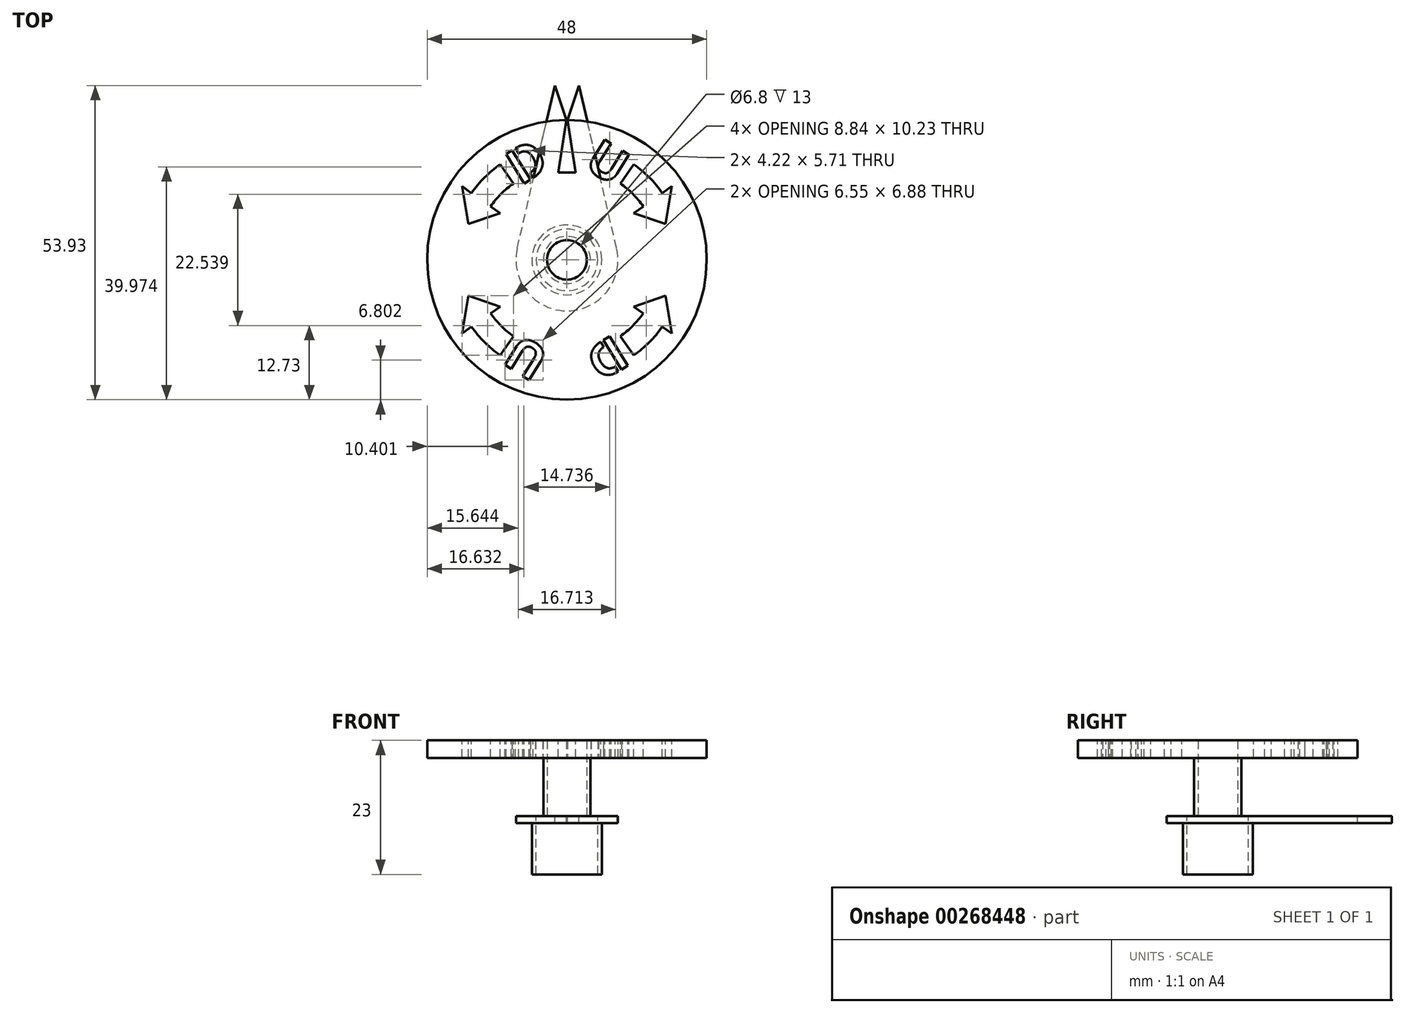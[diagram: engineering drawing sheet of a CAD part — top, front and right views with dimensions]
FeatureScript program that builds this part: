
annotation { "Feature Type Name" : "Feature", "Feature Type Description" : "" }
export const myFeature = defineFeature(function(context is Context, id is Id, definition is map)
    precondition{}
    {
        {
            var Q0;
            Q0=qCreatedBy(makeId("Top.planeOp"),FACE);
            var sketch = newSketch(context, id + "F0", { "sketchPlane" : qUnion([Q0])});
            skCircle(sketch, "E0", {"center": v(0, 0) * mm, "radius": 3.4 * mm});
            skCircle(sketch, "E1", {"center": v(0, 0) * mm, "radius": 4.05 * mm});
            skSolve(sketch);
        }
        {
            var Q0;
            Q0=makeQuery(id+"F0.imprint","IMPRINT",FACE,{"disambiguationData":[TD([[makeQuery(id+"F0.imprint","IMPRINT",EDGE,{"derivedFrom":sQuery(id+"F0.wireOp",EDGE,"E0")}),-1.0]])]});
            extrude(context, id + "F1", {"entities" : qUnion([Q0]), "depth" : 10 * mm, "offsetDistance" : 25 * mm});
        }
        {
            var Q0;
            Q0=makeQuery(id+"F1.opExtrude","CAP_FACE",FACE,{"disambiguationData":[OSD([sQuery(id+"F0.wireOp",EDGE,"E0"),sQuery(id+"F0.wireOp",EDGE,"E1")])],"isStart":false});
            var sketch = newSketch(context, id + "F2", { "sketchPlane" : qUnion([Q0])});
            skCircle(sketch, "E2", {"center": v(0, 0) * mm, "radius": 24 * mm});
            skSolve(sketch);
        }
        {
            var Q0;
            Q0=makeQuery(id+"F2.imprint","IMPRINT",FACE,{"disambiguationData":[TD([[makeQuery(id+"F2.imprint","IMPRINT",EDGE,{"derivedFrom":sQuery(id+"F2.wireOp",EDGE,"E2")}),1.0]])]});
            var Q1;
            Q1=makeQuery(id+"F2.imprint","IMPRINT",FACE,{"disambiguationData":[TD([[makeQuery(id+"F2.imprint","IMPRINT",EDGE,{"derivedFrom":makeQuery(id+"F1.opExtrude","CAP_EDGE",EDGE,{"disambiguationData":[OSD([sQuery(id+"F0.wireOp",EDGE,"E0")])],"isStart":false})}),-1.0]])]});
            extrude(context, id + "F3", {"entities" : qUnion([Q0, Q1]), "operationType" : NewBodyOperationType.ADD, "depth" : 3 * mm, "offsetDistance" : 25 * mm});
        }
        {
            var Q0;
            Q0=makeQuery(id+"F3.opExtrude","CAP_FACE",FACE,{"disambiguationData":[OSD([sQuery(id+"F0.wireOp",EDGE,"E0"),sQuery(id+"F2.wireOp",EDGE,"E2")])],"isStart":false});
            var sketch = newSketch(context, id + "F4", { "sketchPlane" : qUnion([Q0])});
            skLineSegment(sketch, "E3", {"start": v(0, 0) * mm, "end": v(0, 26.54) * mm, "construction": true});
            skLineSegment(sketch, "E4", {"start": v(0, 24.5) * mm, "end": v(-1.5, 15) * mm});
            skLineSegment(sketch, "E5", {"start": v(-1.5, 15) * mm, "end": v(0, 15) * mm});
            skLineSegment(sketch, "E6.MirrorCS", {"start": v(0, 24.5) * mm, "end": v(1.5, 15) * mm});
            skLineSegment(sketch, "E7.MirrorCS", {"start": v(1.5, 15) * mm, "end": v(0, 15) * mm});
            skLineSegment(sketch, "E8", {"start": v(0, 0) * mm, "end": v(22.55, 8.2) * mm, "construction": true});
            skCircle(sketch, "E9", {"center": v(0, 0) * mm, "radius": 18 * mm, "construction": true});
            skLineSegment(sketch, "E10", {"start": v(0, 0) * mm, "end": v(13.77, 19.66) * mm, "construction": true});
            skLineSegment(sketch, "E11", {"start": v(0, 0) * mm, "end": v(19.66, 13.77) * mm, "construction": true});
            skLineSegment(sketch, "E12", {"start": v(10.32, 14.74) * mm, "end": v(11.47, 16.38) * mm});
            skLineSegment(sketch, "E13", {"start": v(10.32, 14.74) * mm, "end": v(9.18, 13.1) * mm});
            skLineSegment(sketch, "E14", {"start": v(11.47, 8.03) * mm, "end": v(13.1, 9.18) * mm});
            skLineSegment(sketch, "E15", {"start": v(13.1, 9.18) * mm, "end": v(14.74, 10.32) * mm});
            skLineSegment(sketch, "E16", {"start": v(14.74, 10.32) * mm, "end": v(16.38, 11.47) * mm});
            skLineSegment(sketch, "E17", {"start": v(16.38, 11.47) * mm, "end": v(18.02, 12.62) * mm});
            skLineSegment(sketch, "E18", {"start": v(11.47, 8.03) * mm, "end": v(16.91, 6.16) * mm});
            skLineSegment(sketch, "E19", {"start": v(16.91, 6.16) * mm, "end": v(18.02, 12.62) * mm});
            skArc(sketch, "E20", {"start": v(13.1, 9.18) * mm, "mid": v(11.31, 11.31) * mm, "end": v(9.18, 13.1) * mm});
            skArc(sketch, "E21", {"start": v(16.38, 11.47) * mm, "mid": v(14.14, 14.14) * mm, "end": v(11.47, 16.38) * mm});
            skText(sketch, "E22", { "text": "U\n", "fontName": "OpenSans-Bold.ttf"});
            skLineSegment(sketch, "E23", {"start": v(0, 0) * mm, "end": v(27.05, 0) * mm, "construction": true});
            skLineSegment(sketch, "E24.MirrorCS", {"start": v(11.47, -8.03) * mm, "end": v(16.91, -6.16) * mm});
            skLineSegment(sketch, "E25.MirrorCS", {"start": v(16.91, -6.16) * mm, "end": v(18.02, -12.62) * mm});
            skArc(sketch, "E26.MirrorCS", {"start": v(13.1, -9.18) * mm, "mid": v(11.31, -11.31) * mm, "end": v(9.18, -13.1) * mm});
            skArc(sketch, "E27.MirrorCS", {"start": v(16.38, -11.47) * mm, "mid": v(14.14, -14.14) * mm, "end": v(11.47, -16.38) * mm});
            skLineSegment(sketch, "E28.MirrorCS", {"start": v(10.32, -14.74) * mm, "end": v(9.18, -13.1) * mm});
            skLineSegment(sketch, "E29.MirrorCS", {"start": v(10.32, -14.74) * mm, "end": v(11.47, -16.38) * mm});
            skLineSegment(sketch, "E30.MirrorCS", {"start": v(11.47, -8.03) * mm, "end": v(13.1, -9.18) * mm});
            skLineSegment(sketch, "E31.MirrorCS", {"start": v(16.38, -11.47) * mm, "end": v(18.02, -12.62) * mm});
            skLineSegment(sketch, "E32.MirrorCS", {"start": v(-10.32, -14.74) * mm, "end": v(-9.18, -13.1) * mm});
            skLineSegment(sketch, "E33.MirrorCS", {"start": v(-10.32, -14.74) * mm, "end": v(-11.47, -16.38) * mm});
            skArc(sketch, "E34.MirrorCS", {"start": v(-16.38, -11.47) * mm, "mid": v(-14.14, -14.14) * mm, "end": v(-11.47, -16.38) * mm});
            skLineSegment(sketch, "E35.MirrorCS", {"start": v(-16.38, -11.47) * mm, "end": v(-18.02, -12.62) * mm});
            skLineSegment(sketch, "E36.MirrorCS", {"start": v(-16.91, -6.16) * mm, "end": v(-18.02, -12.62) * mm});
            skLineSegment(sketch, "E37.MirrorCS", {"start": v(-11.47, -8.03) * mm, "end": v(-16.91, -6.16) * mm});
            skLineSegment(sketch, "E38.MirrorCS", {"start": v(-11.47, -8.03) * mm, "end": v(-13.1, -9.18) * mm});
            skArc(sketch, "E39.MirrorCS", {"start": v(-13.1, -9.18) * mm, "mid": v(-11.31, -11.31) * mm, "end": v(-9.18, -13.1) * mm});
            skLineSegment(sketch, "E40.MirrorCS", {"start": v(-16.91, 6.16) * mm, "end": v(-18.02, 12.62) * mm});
            skLineSegment(sketch, "E41.MirrorCS", {"start": v(-11.47, 8.03) * mm, "end": v(-16.91, 6.16) * mm});
            skLineSegment(sketch, "E42.MirrorCS", {"start": v(-11.47, 8.03) * mm, "end": v(-13.1, 9.18) * mm});
            skArc(sketch, "E43.MirrorCS", {"start": v(-13.1, 9.18) * mm, "mid": v(-11.31, 11.31) * mm, "end": v(-9.18, 13.1) * mm});
            skLineSegment(sketch, "E44.MirrorCS", {"start": v(-10.32, 14.74) * mm, "end": v(-9.18, 13.1) * mm});
            skLineSegment(sketch, "E45.MirrorCS", {"start": v(-10.32, 14.74) * mm, "end": v(-11.47, 16.38) * mm});
            skArc(sketch, "E46.MirrorCS", {"start": v(-16.38, 11.47) * mm, "mid": v(-14.14, 14.14) * mm, "end": v(-11.47, 16.38) * mm});
            skLineSegment(sketch, "E47.MirrorCS", {"start": v(-16.38, 11.47) * mm, "end": v(-18.02, 12.62) * mm});
            skText(sketch, "E48", { "text": "D", "fontName": "OpenSans-Bold.ttf"});
            skText(sketch, "E49", { "text": "U", "fontName": "OpenSans-Bold.ttf"});
            skPoint(sketch, "E49.firstSnap0", {"position": v(11.31, -11.31) * mm});
            skText(sketch, "E50", { "text": "D", "fontName": "OpenSans-Bold.ttf"});
            skLineSegment(sketch, "E51", {"start": v(0, 0) * mm, "end": v(12.72, -20.35) * mm, "construction": true});
            skLineSegment(sketch, "E52", {"start": v(0, 0) * mm, "end": v(-12.72, -20.35) * mm, "construction": true});
            skLineSegment(sketch, "E53", {"start": v(0, 0) * mm, "end": v(12.72, 20.35) * mm, "construction": true});
            skLineSegment(sketch, "E54", {"start": v(0, 0) * mm, "end": v(-12.72, 20.35) * mm, "construction": true});
            const initialGuessF4  = {"E22": [0.00275, 0.01597, 0.84805, -0.52992, 0.006], "E48": [-0.00795, 0.01272, 0.84805, 0.52992, 0.006], "E49": [-0.00275, -0.01597, -0.84805, 0.52992, 0.006], "E50": [0.00795, -0.01272, -0.84805, -0.52992, 0.006]};
            skSetInitialGuess(sketch, initialGuessF4);
            skSolve(sketch);
        }
        {
            var Q0;
            {var subQ4=sQuery(id+"F4.wireOp",EDGE,"E5");Q0=makeQuery(id+"F4.imprint","IMPRINT",FACE,{"disambiguationData":[TD([[makeQuery(id+"F4.imprint","IMPRINT",EDGE,{"derivedFrom":subQ4}),1.0]])]});}
            var Q1;
            {var subQ0=sQuery(id+"F4.wireOp",EDGE,"E6.MirrorCS");var subQ1=sQuery(id+"F4.wireOp",EDGE,"E4");var subQ2=makeQuery(id+"F4.imprint","INTERSECT",VERTEX,{"derivedFrom":[subQ1,subQ0]});Q1=makeQuery(id+"F4.imprint","IMPRINT",FACE,{"disambiguationData":[TD([[makeQuery(id+"F4.imprint","IMPRINT",EDGE,{"disambiguationData":[TD([[subQ2,-1.0]])],"derivedFrom":subQ1}),1.0]])]});}
            var Q2;
            Q2=makeQuery(id+"F4.imprint","IMPRINT",FACE,{"disambiguationData":[TD([[makeQuery(id+"F4.imprint","IMPRINT",EDGE,{"derivedFrom":sQuery(id+"F4.wireOp",EDGE,"E12")}),-1.0]])]});
            var Q3;
            Q3=makeQuery(id+"F4.imprint","IMPRINT",FACE,{"disambiguationData":[TD([[makeQuery(id+"F4.imprint","IMPRINT",EDGE,{"derivedFrom":sQuery(id+"F4.wireOp",EDGE,"E14")}),-1.0]])]});
            var Q4;
            Q4=makeQuery(id+"F4.imprint","IMPRINT",FACE,{"disambiguationData":[TD([[makeQuery(id+"F4.imprint","IMPRINT",EDGE,{"derivedFrom":sQuery(id+"F4.wireOp",EDGE,"E22.sketch_text.stroke-0")}),-1.0]])]});
            var Q5;
            Q5=makeQuery(id+"F4.imprint","IMPRINT",FACE,{"disambiguationData":[TD([[makeQuery(id+"F4.imprint","IMPRINT",EDGE,{"derivedFrom":sQuery(id+"F4.wireOp",EDGE,"E40.MirrorCS")}),-1.0]])]});
            var Q6;
            Q6=makeQuery(id+"F4.imprint","IMPRINT",FACE,{"disambiguationData":[TD([[makeQuery(id+"F4.imprint","IMPRINT",EDGE,{"derivedFrom":sQuery(id+"F4.wireOp",EDGE,"E32.MirrorCS")}),1.0]])]});
            var Q7;
            Q7=makeQuery(id+"F4.imprint","IMPRINT",FACE,{"disambiguationData":[TD([[makeQuery(id+"F4.imprint","IMPRINT",EDGE,{"derivedFrom":sQuery(id+"F4.wireOp",EDGE,"E24.MirrorCS")}),-1.0]])]});
            var Q8;
            Q8=makeQuery(id+"F4.imprint","IMPRINT",FACE,{"disambiguationData":[TD([[makeQuery(id+"F4.imprint","IMPRINT",EDGE,{"derivedFrom":sQuery(id+"F4.wireOp",EDGE,"E48.sketch_text.stroke-0")}),-1.0]])]});
            var Q9;
            Q9=makeQuery(id+"F4.imprint","IMPRINT",FACE,{"disambiguationData":[TD([[makeQuery(id+"F4.imprint","IMPRINT",EDGE,{"derivedFrom":sQuery(id+"F4.wireOp",EDGE,"E50.sketch_text.stroke-0")}),-1.0]])]});
            var Q10;
            Q10=makeQuery(id+"F4.imprint","IMPRINT",FACE,{"disambiguationData":[TD([[makeQuery(id+"F4.imprint","IMPRINT",EDGE,{"derivedFrom":sQuery(id+"F4.wireOp",EDGE,"E49.sketch_text.stroke-0")}),-1.0]])]});
            var Q11;
            Q11=makeQuery(id+"F3.opExtrude","CAP_FACE",FACE,{"disambiguationData":[OSD([sQuery(id+"F0.wireOp",EDGE,"E0"),sQuery(id+"F2.wireOp",EDGE,"E2")])],"isStart":true});
            extrude(context, id + "F5", {"entities" : qUnion([Q0, Q1, Q2, Q3, Q4, Q5, Q6, Q7, Q8, Q9, Q10]), "operationType" : NewBodyOperationType.REMOVE, "endBound" : BoundingType.UP_TO_SURFACE, "oppositeDirection" : true, "depth" : 25 * mm, "endBoundEntityFace" : qUnion([Q11]), "offsetDistance" : 25 * mm});
        }
        {
            var Q0;
            Q0=makeQuery(id+"F5.boolean.opBoolean","COPY",FACE,{"derivedFrom":makeQuery(id+"F5.opExtrude","SWEPT_FACE",FACE,{"disambiguationData":[OSD([sQuery(id+"F4.wireOp",EDGE,"E48.sketch_text.stroke-10")])]})});
            extrude(context, id + "F6", {"entities" : qUnion([Q0]), "operationType" : NewBodyOperationType.ADD, "endBound" : BoundingType.UP_TO_NEXT, "depth" : 25 * mm, "offsetDistance" : 25 * mm});
        }
        {
            var Q0;
            Q0=makeQuery(id+"F5.boolean.opBoolean","COPY",FACE,{"derivedFrom":makeQuery(id+"F5.opExtrude","SWEPT_FACE",FACE,{"disambiguationData":[OSD([sQuery(id+"F4.wireOp",EDGE,"E48.sketch_text.stroke-8")])]})});
            extrude(context, id + "F7", {"entities" : qUnion([Q0]), "operationType" : NewBodyOperationType.ADD, "endBound" : BoundingType.UP_TO_NEXT, "depth" : 25 * mm, "offsetDistance" : 25 * mm});
        }
        {
            var Q0;
            Q0=makeQuery(id+"F5.boolean.opBoolean","COPY",FACE,{"derivedFrom":makeQuery(id+"F5.opExtrude","SWEPT_FACE",FACE,{"disambiguationData":[OSD([sQuery(id+"F4.wireOp",EDGE,"E50.sketch_text.stroke-8")])]})});
            extrude(context, id + "F8", {"entities" : qUnion([Q0]), "operationType" : NewBodyOperationType.ADD, "endBound" : BoundingType.UP_TO_NEXT, "depth" : 25 * mm, "offsetDistance" : 25 * mm});
        }
        {
            var Q0;
            Q0=makeQuery(id+"F5.boolean.opBoolean","COPY",FACE,{"derivedFrom":makeQuery(id+"F5.opExtrude","SWEPT_FACE",FACE,{"disambiguationData":[OSD([sQuery(id+"F4.wireOp",EDGE,"E50.sketch_text.stroke-10")])]})});
            extrude(context, id + "F9", {"entities" : qUnion([Q0]), "operationType" : NewBodyOperationType.ADD, "endBound" : BoundingType.UP_TO_NEXT, "depth" : 25 * mm, "offsetDistance" : 25 * mm});
        }
        {
            var Q0;
            Q0=qCreatedBy(makeId("Top.planeOp"),FACE);
            var sketch = newSketch(context, id + "F10", { "sketchPlane" : qUnion([Q0])});
            skCircle(sketch, "E55", {"center": v(0, 0) * mm, "radius": 5.28 * mm});
            skCircle(sketch, "E56", {"center": v(0, 0) * mm, "radius": 6 * mm});
            skCircle(sketch, "E57", {"center": v(0, 0) * mm, "radius": 8.75 * mm});
            skLineSegment(sketch, "E58", {"start": v(0, 0) * mm, "end": v(0, 34.02) * mm, "construction": true});
            skLineSegment(sketch, "E59", {"start": v(0, 0) * mm, "end": v(-2.35, 33.56) * mm, "construction": true});
            skLineSegment(sketch, "E60", {"start": v(0, 0) * mm, "end": v(2.4, 34.43) * mm, "construction": true});
            skCircle(sketch, "E61", {"center": v(0, 0) * mm, "radius": 30 * mm});
            skLineSegment(sketch, "E62", {"start": v(-8.53, 1.96) * mm, "end": v(-2.1, 29.93) * mm});
            skLineSegment(sketch, "E63", {"start": v(8.53, 1.96) * mm, "end": v(2.1, 29.93) * mm});
            skPoint(sketch, "E64.0", {"position": v(-0.08, 24) * mm});
            skPoint(sketch, "E64.1", {"position": v(0.08, 24) * mm});
            skLineSegment(sketch, "E65", {"start": v(-2.1, 29.93) * mm, "end": v(-0.08, 24) * mm});
            skLineSegment(sketch, "E66", {"start": v(-0.08, 24) * mm, "end": v(0.08, 24) * mm});
            skLineSegment(sketch, "E67", {"start": v(0.08, 24) * mm, "end": v(2.1, 29.93) * mm});
            skSolve(sketch);
        }
        {
            var Q0;
            Q0=makeQuery(id+"F10.imprint","IMPRINT",FACE,{"disambiguationData":[TD([[makeQuery(id+"F10.imprint","IMPRINT",EDGE,{"derivedFrom":sQuery(id+"F10.wireOp",EDGE,"E56")}),-1.0]])]});
            var Q1;
            {var subQ0=sQuery(id+"F10.wireOp",EDGE,"E62");Q1=makeQuery(id+"F10.imprint","IMPRINT",FACE,{"disambiguationData":[TD([[makeQuery(id+"F10.imprint","IMPRINT",EDGE,{"derivedFrom":subQ0}),-1.0]])]});}
            extrude(context, id + "F11", {"entities" : qUnion([Q0, Q1]), "oppositeDirection" : true, "depth" : 1.2 * mm, "offsetDistance" : 25 * mm});
        }
        {
            var Q0;
            Q0=makeQuery(id+"F10.imprint","IMPRINT",FACE,{"disambiguationData":[TD([[makeQuery(id+"F10.imprint","IMPRINT",EDGE,{"derivedFrom":sQuery(id+"F10.wireOp",EDGE,"E55")}),-1.0]])]});
            extrude(context, id + "F12", {"entities" : qUnion([Q0]), "operationType" : NewBodyOperationType.ADD, "oppositeDirection" : true, "depth" : 10 * mm, "offsetDistance" : 25 * mm});
        }
    });
